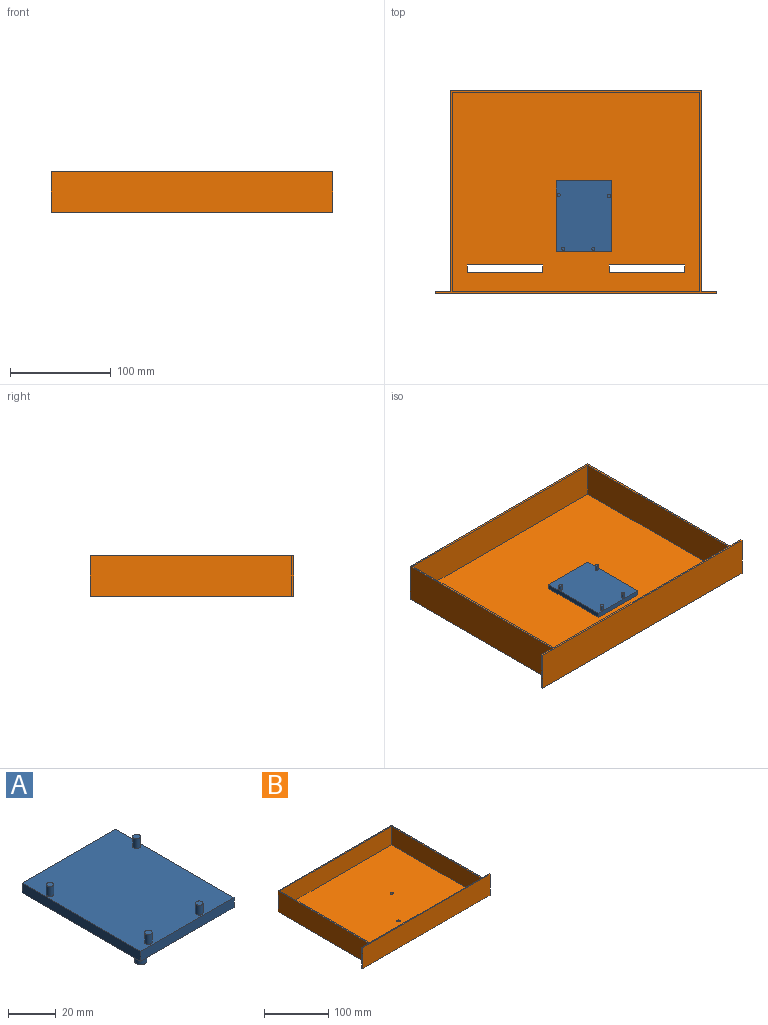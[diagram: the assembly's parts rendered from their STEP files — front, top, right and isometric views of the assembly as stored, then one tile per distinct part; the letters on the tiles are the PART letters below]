
ASSEMBLY  parts=2 mates=1
PART A: 18 faces, bbox 55x70x15 mm
  f0: plane 70x5mm, normal (-1,0,0), area 350mm2, adj f1,f3,f4,f5
  f1: plane 55x5mm, normal (0,-1,0), area 275mm2, adj f0,f2,f4,f5
  f2: plane 70x5mm, normal (1,0,0), area 350mm2, adj f1,f3,f4,f5
  f3: plane 55x5mm, normal (0,1,0), area 275mm2, adj f0,f2,f4,f5
  f4: plane 70x55mm, normal (0,0,-1), area 3810.7mm2, adj f0,f1,f2,f3,f14,f16
  f5: plane 70x55mm, normal (0,0,1), area 3818.8mm2, adj f0,f1,f2,f3,f6,f8,f10,f12
  f6: cylinder r=1.57mm len=5mm, axis (0,0,-1), area 49.5mm2, adj f5,f7
  f7: plane 3.15x3.15mm, normal (0,0,1), area 7.8mm2, adj f6
  f8: cylinder r=1.57mm len=5mm, axis (0,0,-1), area 49.5mm2, adj f5,f9
  f9: plane 3.15x3.15mm, normal (0,0,1), area 7.8mm2, adj f8
  f10: cylinder r=1.57mm len=5mm, axis (0,0,-1), area 49.5mm2, adj f5,f11
  f11: plane 3.15x3.15mm, normal (0,0,1), area 7.8mm2, adj f10
  f12: cylinder r=1.57mm len=5mm, axis (0,0,-1), area 49.5mm2, adj f5,f13
  f13: plane 3.15x3.15mm, normal (0,0,1), area 7.8mm2, adj f12
  f14: cylinder r=2.5mm len=5mm, axis (0,0,1), area 78.5mm2, adj f4,f15
  f15: plane 5x5mm, normal (0,0,-1), area 19.6mm2, adj f14
  f16: cylinder r=2.5mm len=5mm, axis (0,0,1), area 78.5mm2, adj f4,f17
  f17: plane 5x5mm, normal (0,0,-1), area 19.6mm2, adj f16
PART B: 25 faces, bbox 280x202x40 mm
  f0: plane 246x198mm, normal (0,0,1), area 47479.4mm2, adj f11,f12,f13,f14,f15,f16,f17,f18
  f1: plane 280x202mm, normal (0,0,1), area 1852mm2, adj f2,f3,f4,f5,f6,f7,f8,f9
  f2: plane 250x40mm, normal (0,1,0), area 10000mm2, adj f1,f3,f9,f10
  f3: plane 200x40mm, normal (-1,0,0), area 8000mm2, adj f1,f2,f4,f10
  f4: plane 40x15mm, normal (0,1,0), area 600mm2, adj f1,f3,f5,f10
  f5: plane 40x2mm, normal (-1,0,0), area 80mm2, adj f1,f4,f6,f10
  f6: plane 280x40mm, normal (0,-1,0), area 11200mm2, adj f1,f5,f7,f10
  f7: plane 40x2mm, normal (1,0,0), area 80mm2, adj f1,f6,f8,f10
  f8: plane 40x15mm, normal (0,1,0), area 600mm2, adj f1,f7,f9,f10
  f9: plane 200x40mm, normal (1,0,0), area 8000mm2, adj f1,f2,f8,f10
  f10: plane 280x202mm, normal (0,0,-1), area 49331.4mm2, adj f2,f3,f4,f5,f6,f7,f8,f9
  f11: plane 246x35mm, normal (0,-1,0), area 8610mm2, adj f0,f1,f12,f14
  f12: plane 198x35mm, normal (1,0,0), area 6930mm2, adj f0,f1,f11,f13
  f13: plane 246x35mm, normal (0,1,0), area 8610mm2, adj f0,f1,f12,f14
  f14: plane 198x35mm, normal (-1,0,0), area 6930mm2, adj f0,f1,f11,f13
  f15: plane 7.93x5mm, normal (1,0,0), area 39.6mm2, adj f0,f10,f16,f17
  f16: plane 75x5mm, normal (0,-1,0), area 375mm2, adj f0,f10,f15,f18
  f17: plane 75x5mm, normal (0,1,0), area 375mm2, adj f0,f10,f15,f18
  f18: plane 7.93x5mm, normal (-1,0,0), area 39.6mm2, adj f0,f10,f16,f17
  f19: plane 7.93x5mm, normal (1,0,0), area 39.6mm2, adj f0,f10,f20,f21
  f20: plane 75x5mm, normal (0,-1,0), area 375mm2, adj f0,f10,f19,f22
  f21: plane 75x5mm, normal (0,1,0), area 375mm2, adj f0,f10,f19,f22
  f22: plane 7.93x5mm, normal (-1,0,0), area 39.6mm2, adj f0,f10,f20,f21
  f23: cylinder r=2.5mm len=5mm, axis (0,0,1), area 78.5mm2, adj f0,f10
  f24: cylinder r=2.5mm len=5mm, axis (0,0,1), area 78.5mm2, adj f0,f10
PLACE A t=(72.8,5.93,-14.43)mm
PLACE B t=(69.64,53.92,-24.43)mm fixed
MATE cylindrical A.f14 <-> B.f24  axis (0,0,-1) through (31.56,-49.7,-24.43)mm
